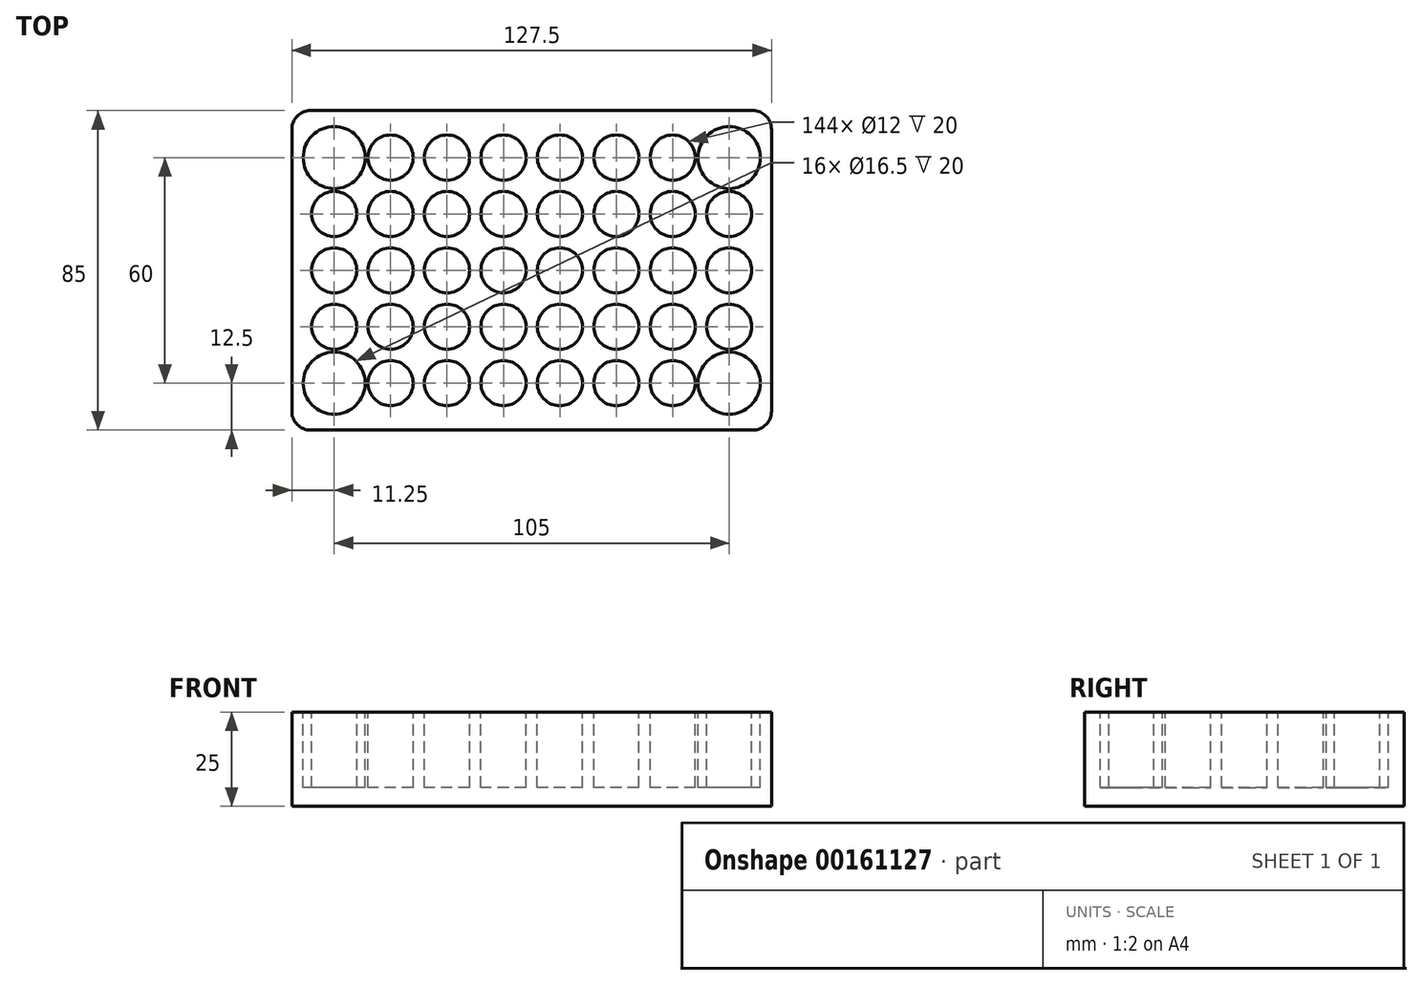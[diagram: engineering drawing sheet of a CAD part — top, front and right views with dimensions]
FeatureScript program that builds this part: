
annotation { "Feature Type Name" : "Feature", "Feature Type Description" : "" }
export const myFeature = defineFeature(function(context is Context, id is Id, definition is map)
    precondition{}
    {
        {
            var Q0;
            Q0=qCreatedBy(makeId("Top.planeOp"),FACE);
            var sketch = newSketch(context, id + "F0", { "sketchPlane" : qUnion([Q0])});
            skLineSegment(sketch, "E0.bottom", {"start": v(58.75, -42.5) * mm, "end": v(-58.75, -42.5) * mm});
            skLineSegment(sketch, "E0.top", {"start": v(58.75, 42.5) * mm, "end": v(-58.75, 42.5) * mm});
            skLineSegment(sketch, "E0.left", {"start": v(63.75, -37.5) * mm, "end": v(63.75, 37.5) * mm});
            skLineSegment(sketch, "E0.right", {"start": v(-63.75, -37.5) * mm, "end": v(-63.75, 37.5) * mm});
            skPoint(sketch, "E0.middle", {"position": v(0, 0) * mm});
            skPoint(sketch, "E1.visualSharp", {"position": v(-63.75, 42.5) * mm});
            skArc(sketch, "E1.filletArc", {"start": v(-58.75, 42.5) * mm, "mid": v(-62.29, 41.04) * mm, "end": v(-63.75, 37.5) * mm});
            skPoint(sketch, "E2.visualSharp", {"position": v(-63.75, -42.5) * mm});
            skArc(sketch, "E2.filletArc", {"start": v(-63.75, -37.5) * mm, "mid": v(-62.29, -41.04) * mm, "end": v(-58.75, -42.5) * mm});
            skPoint(sketch, "E3.visualSharp", {"position": v(63.75, -42.5) * mm});
            skArc(sketch, "E3.filletArc", {"start": v(58.75, -42.5) * mm, "mid": v(62.29, -41.04) * mm, "end": v(63.75, -37.5) * mm});
            skPoint(sketch, "E4.visualSharp", {"position": v(63.75, 42.5) * mm});
            skArc(sketch, "E4.filletArc", {"start": v(63.75, 37.5) * mm, "mid": v(62.29, 41.04) * mm, "end": v(58.75, 42.5) * mm});
            skSolve(sketch);
        }
        {
            var Q0;
            Q0=qSketchRegion(id+"F0",true);
            extrude(context, id + "F1", {"entities" : qUnion([Q0]), "depth" : 25 * mm});
        }
        {
            var Q0;
            Q0=makeQuery(id+"F1.opExtrude","CAP_FACE",FACE,{"disambiguationData":[OSD([sQuery(id+"F0.wireOp",EDGE,"E0.bottom"),sQuery(id+"F0.wireOp",EDGE,"E0.top"),sQuery(id+"F0.wireOp",EDGE,"E0.left"),sQuery(id+"F0.wireOp",EDGE,"E0.right"),sQuery(id+"F0.wireOp",EDGE,"E1.filletArc"),sQuery(id+"F0.wireOp",EDGE,"E2.filletArc"),sQuery(id+"F0.wireOp",EDGE,"E3.filletArc"),sQuery(id+"F0.wireOp",EDGE,"E4.filletArc")])],"isStart":false});
            var sketch = newSketch(context, id + "F2", { "sketchPlane" : qUnion([Q0])});
            skCircle(sketch, "E5.0.1.0", {"center": v(-52.5, 15) * mm, "radius": 6 * mm});
            skCircle(sketch, "E5.0.2.0", {"center": v(-52.5, 0) * mm, "radius": 6 * mm});
            skCircle(sketch, "E5.0.3.0", {"center": v(-52.5, -15) * mm, "radius": 6 * mm});
            skCircle(sketch, "E5.1.0.0", {"center": v(-37.5, 30) * mm, "radius": 6 * mm});
            skCircle(sketch, "E5.1.1.0", {"center": v(-37.5, 15) * mm, "radius": 6 * mm});
            skCircle(sketch, "E5.1.2.0", {"center": v(-37.5, 0) * mm, "radius": 6 * mm});
            skCircle(sketch, "E5.1.3.0", {"center": v(-37.5, -15) * mm, "radius": 6 * mm});
            skCircle(sketch, "E5.1.4.0", {"center": v(-37.5, -30) * mm, "radius": 6 * mm});
            skCircle(sketch, "E5.2.0.0", {"center": v(-22.5, 30) * mm, "radius": 6 * mm});
            skCircle(sketch, "E5.2.1.0", {"center": v(-22.5, 15) * mm, "radius": 6 * mm});
            skCircle(sketch, "E5.2.2.0", {"center": v(-22.5, 0) * mm, "radius": 6 * mm});
            skCircle(sketch, "E5.2.3.0", {"center": v(-22.5, -15) * mm, "radius": 6 * mm});
            skCircle(sketch, "E5.2.4.0", {"center": v(-22.5, -30) * mm, "radius": 6 * mm});
            skCircle(sketch, "E5.3.0.0", {"center": v(-7.5, 30) * mm, "radius": 6 * mm});
            skCircle(sketch, "E5.3.1.0", {"center": v(-7.5, 15) * mm, "radius": 6 * mm});
            skCircle(sketch, "E5.3.2.0", {"center": v(-7.5, 0) * mm, "radius": 6 * mm});
            skCircle(sketch, "E5.3.3.0", {"center": v(-7.5, -15) * mm, "radius": 6 * mm});
            skCircle(sketch, "E5.3.4.0", {"center": v(-7.5, -30) * mm, "radius": 6 * mm});
            skCircle(sketch, "E5.4.0.0", {"center": v(7.5, 30) * mm, "radius": 6 * mm});
            skCircle(sketch, "E5.4.1.0", {"center": v(7.5, 15) * mm, "radius": 6 * mm});
            skCircle(sketch, "E5.4.2.0", {"center": v(7.5, 0) * mm, "radius": 6 * mm});
            skCircle(sketch, "E5.4.3.0", {"center": v(7.5, -15) * mm, "radius": 6 * mm});
            skCircle(sketch, "E5.4.4.0", {"center": v(7.5, -30) * mm, "radius": 6 * mm});
            skCircle(sketch, "E5.5.0.0", {"center": v(22.5, 30) * mm, "radius": 6 * mm});
            skCircle(sketch, "E5.5.1.0", {"center": v(22.5, 15) * mm, "radius": 6 * mm});
            skCircle(sketch, "E5.5.2.0", {"center": v(22.5, 0) * mm, "radius": 6 * mm});
            skCircle(sketch, "E5.5.3.0", {"center": v(22.5, -15) * mm, "radius": 6 * mm});
            skCircle(sketch, "E5.5.4.0", {"center": v(22.5, -30) * mm, "radius": 6 * mm});
            skCircle(sketch, "E5.6.0.0", {"center": v(37.5, 30) * mm, "radius": 6 * mm});
            skCircle(sketch, "E5.6.1.0", {"center": v(37.5, 15) * mm, "radius": 6 * mm});
            skCircle(sketch, "E5.6.2.0", {"center": v(37.5, 0) * mm, "radius": 6 * mm});
            skCircle(sketch, "E5.6.3.0", {"center": v(37.5, -15) * mm, "radius": 6 * mm});
            skCircle(sketch, "E5.6.4.0", {"center": v(37.5, -30) * mm, "radius": 6 * mm});
            skCircle(sketch, "E5.7.1.0", {"center": v(52.5, 15) * mm, "radius": 6 * mm});
            skCircle(sketch, "E5.7.2.0", {"center": v(52.5, 0) * mm, "radius": 6 * mm});
            skCircle(sketch, "E5.7.3.0", {"center": v(52.5, -15) * mm, "radius": 6 * mm});
            skLineSegment(sketch, "E5.direction1", {"start": v(-52.5, 30) * mm, "end": v(-37.5, 30) * mm, "construction": true});
            skLineSegment(sketch, "E5.direction2", {"start": v(-52.5, 30) * mm, "end": v(-52.5, 15) * mm, "construction": true});
            skCircle(sketch, "E6", {"center": v(-52.5, 30) * mm, "radius": 8.25 * mm});
            skCircle(sketch, "E7", {"center": v(-52.5, -30) * mm, "radius": 8.25 * mm});
            skCircle(sketch, "E8", {"center": v(52.5, 30) * mm, "radius": 8.25 * mm});
            skCircle(sketch, "E9", {"center": v(52.5, -30) * mm, "radius": 8.25 * mm});
            skSolve(sketch);
        }
        {
            var Q0;
            Q0=qSketchRegion(id+"F2",true);
            extrude(context, id + "F3", {"entities" : qUnion([Q0]), "operationType" : NewBodyOperationType.REMOVE, "oppositeDirection" : true, "depth" : 20 * mm});
        }
    });
